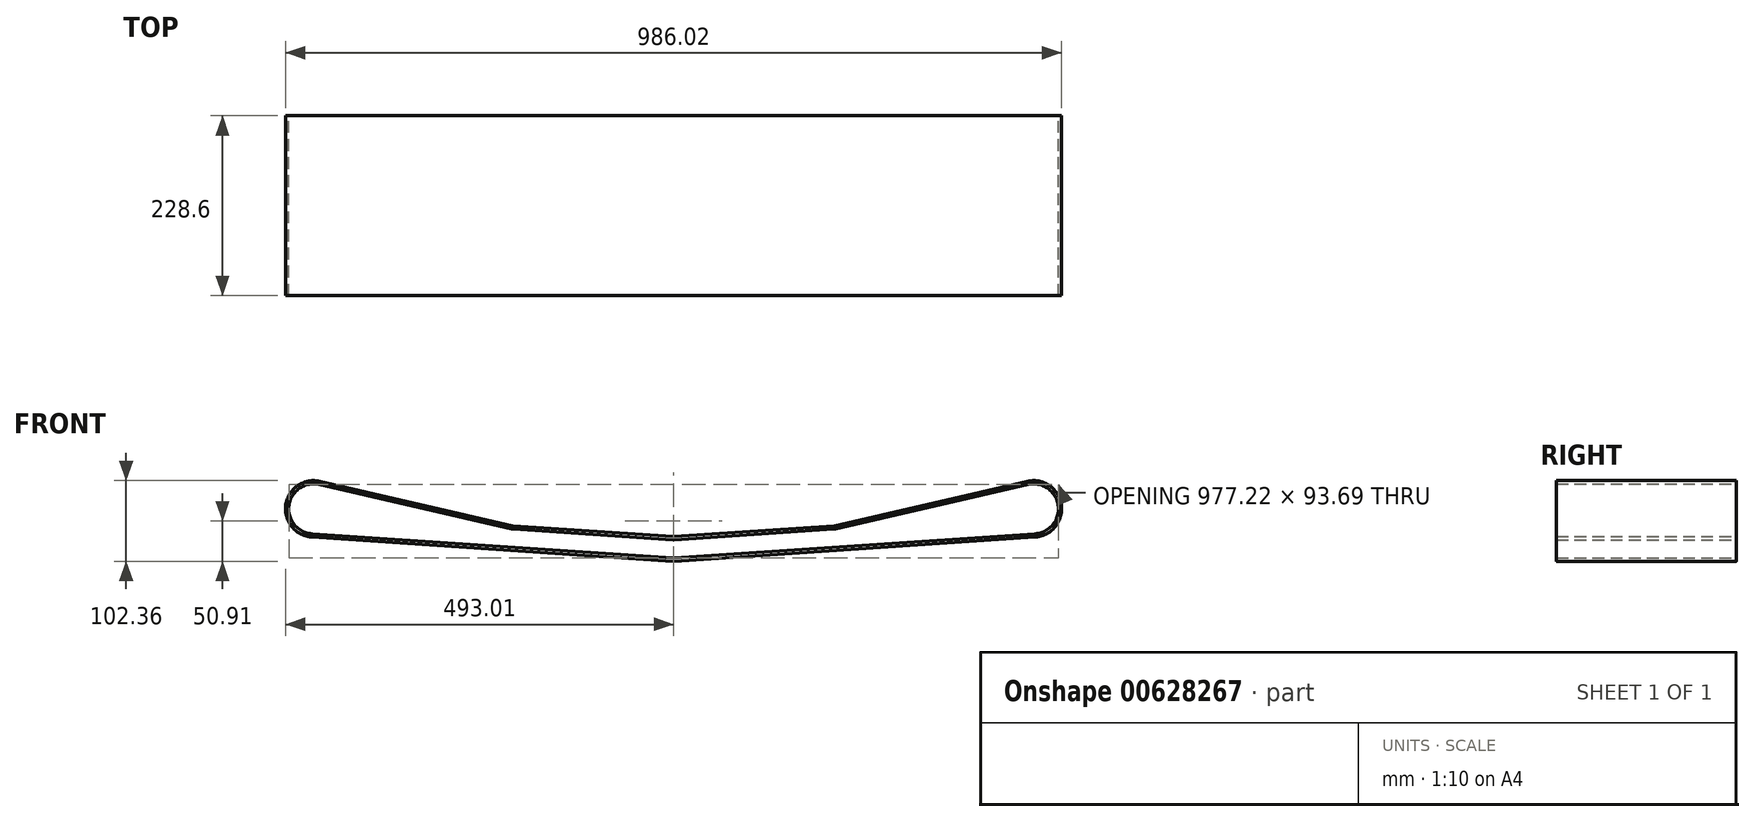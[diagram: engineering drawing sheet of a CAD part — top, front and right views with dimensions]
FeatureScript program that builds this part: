
annotation { "Feature Type Name" : "Feature", "Feature Type Description" : "" }
export const myFeature = defineFeature(function(context is Context, id is Id, definition is map)
    precondition{}
    {
        {
            var Q0;
            Q0=qCreatedBy(makeId("Front.planeOp"),FACE);
            var sketch = newSketch(context, id + "F0", { "sketchPlane" : qUnion([Q0])});
            skArc(sketch, "E0", {"start": v(7.14, 30.94) * mm, "mid": v(-31.4, 4.65) * mm, "end": v(-2.13, -31.68) * mm});
            skLineSegment(sketch, "E1.MirrorCS", {"start": v(907.26, 30.94) * mm, "end": v(662.74, -25.51) * mm});
            skArc(sketch, "E2.MirrorC", {"start": v(907.26, 30.94) * mm, "mid": v(945.8, 4.65) * mm, "end": v(916.53, -31.68) * mm});
            skCircle(sketch, "E3", {"center": v(-76.2, 0) * mm, "radius": 6.35 * mm});
            skCircle(sketch, "E4", {"center": v(254, -15.37) * mm, "radius": 10.41 * mm});
            skCircle(sketch, "E5", {"center": v(457.2, -28.96) * mm, "radius": 10.41 * mm});
            skCircle(sketch, "E6", {"center": v(660.4, -15.37) * mm, "radius": 10.41 * mm});
            skLineSegment(sketch, "E7", {"start": v(-76.2, 0) * mm, "end": v(914.4, 0) * mm, "construction": true});
            skLineSegment(sketch, "E8", {"start": v(0, -31.75) * mm, "end": v(914.4, -31.75) * mm, "construction": true});
            skLineSegment(sketch, "E9", {"start": v(7.14, 30.94) * mm, "end": v(251.66, -25.51) * mm});
            skLineSegment(sketch, "E10", {"start": v(253.3, -25.76) * mm, "end": v(456.5, -39.35) * mm});
            skLineSegment(sketch, "E11", {"start": v(457.9, -39.35) * mm, "end": v(661.1, -25.76) * mm});
            skCircle(sketch, "E12", {"center": v(457.2, -56.13) * mm, "radius": 6.35 * mm});
            skPoint(sketch, "E13.centerSnap0", {"position": v(457.2, -31.75) * mm});
            skCircle(sketch, "E14", {"center": v(457.2, 654.74) * mm, "radius": 635 * mm});
            skLineSegment(sketch, "E15", {"start": v(-2.13, -31.68) * mm, "end": v(456.77, -62.47) * mm});
            skLineSegment(sketch, "E16", {"start": v(457.63, -62.47) * mm, "end": v(916.53, -31.68) * mm});
            skArc(sketch, "E17", {"start": v(-2.13, -31.68) * mm, "mid": v(-1.06, -31.73) * mm, "end": v(0, -31.75) * mm, "construction": true});
            skArc(sketch, "E18", {"start": v(916.53, -31.68) * mm, "mid": v(915.46, -31.73) * mm, "end": v(914.4, -31.75) * mm, "construction": true});
            skSolve(sketch);
        }
        {
            var Q0;
            Q0=qCreatedBy(makeId("Front.planeOp"), FACE);
            var sketch = newSketch(context, id + "F1", { "sketchPlane" : qUnion([Q0])});
            skLineSegment(sketch, "E19.0", {"start": v(7.14, 30.94) * mm, "end": v(251.66, -25.51) * mm});
            skLineSegment(sketch, "E19.1", {"start": v(253.3, -25.76) * mm, "end": v(456.5, -39.35) * mm});
            skArc(sketch, "E19.2", {"start": v(251.66, -25.51) * mm, "mid": v(252.48, -25.67) * mm, "end": v(253.3, -25.76) * mm});
            skLineSegment(sketch, "E19.3", {"start": v(457.9, -39.35) * mm, "end": v(661.1, -25.76) * mm});
            skArc(sketch, "E19.4", {"start": v(456.5, -39.35) * mm, "mid": v(457.2, -39.37) * mm, "end": v(457.9, -39.35) * mm});
            skArc(sketch, "E19.5", {"start": v(661.1, -25.76) * mm, "mid": v(661.92, -25.67) * mm, "end": v(662.74, -25.51) * mm});
            skLineSegment(sketch, "E19.6", {"start": v(907.26, 30.94) * mm, "end": v(662.74, -25.51) * mm});
            skArc(sketch, "E19.8", {"start": v(7.14, 30.94) * mm, "mid": v(-31.4, 4.65) * mm, "end": v(-2.13, -31.68) * mm});
            skArc(sketch, "E19.9", {"start": v(907.26, 30.94) * mm, "mid": v(945.8, 4.65) * mm, "end": v(916.53, -31.68) * mm});
            skArc(sketch, "E20.0", {"start": v(456.78, -35.3) * mm, "mid": v(457.2, -35.3) * mm, "end": v(457.62, -35.3) * mm});
            skLineSegment(sketch, "E20.1", {"start": v(457.62, -35.3) * mm, "end": v(660.82, -21.7) * mm});
            skArc(sketch, "E20.2", {"start": v(660.82, -21.7) * mm, "mid": v(661.33, -21.65) * mm, "end": v(661.83, -21.55) * mm});
            skLineSegment(sketch, "E20.3", {"start": v(906.34, 34.9) * mm, "end": v(661.83, -21.55) * mm});
            skLineSegment(sketch, "E20.7", {"start": v(8.06, 34.9) * mm, "end": v(252.57, -21.55) * mm});
            skArc(sketch, "E20.8", {"start": v(252.57, -21.55) * mm, "mid": v(253.07, -21.65) * mm, "end": v(253.58, -21.7) * mm});
            skLineSegment(sketch, "E20.9", {"start": v(253.58, -21.7) * mm, "end": v(456.78, -35.3) * mm});
            skLineSegment(sketch, "E21.0", {"start": v(457.63, -62.47) * mm, "end": v(916.53, -31.68) * mm});
            skArc(sketch, "E21.1", {"start": v(456.77, -62.47) * mm, "mid": v(457.2, -62.48) * mm, "end": v(457.63, -62.47) * mm});
            skLineSegment(sketch, "E21.2", {"start": v(-2.13, -31.68) * mm, "end": v(456.77, -62.47) * mm});
            skArc(sketch, "E22.0", {"start": v(8.06, 34.9) * mm, "mid": v(-35.43, 5.24) * mm, "end": v(-2.4, -35.73) * mm});
            skLineSegment(sketch, "E22.1", {"start": v(-2.4, -35.73) * mm, "end": v(456.5, -66.52) * mm});
            skArc(sketch, "E22.2", {"start": v(456.5, -66.52) * mm, "mid": v(457.2, -66.55) * mm, "end": v(457.9, -66.52) * mm});
            skLineSegment(sketch, "E22.3", {"start": v(457.9, -66.52) * mm, "end": v(916.8, -35.73) * mm});
            skArc(sketch, "E22.4", {"start": v(906.34, 34.9) * mm, "mid": v(949.83, 5.24) * mm, "end": v(916.8, -35.73) * mm});
            skSolve(sketch);
        }
        {
            var Q0;
            Q0 = qSketchRegion(id + "F1", true);
            extrude(context, id + "F2", {"entities" : qUnion([Q0]), "depth" : 228.6 * mm, "offsetDistance" : 25.4 * mm});
        }
    });
